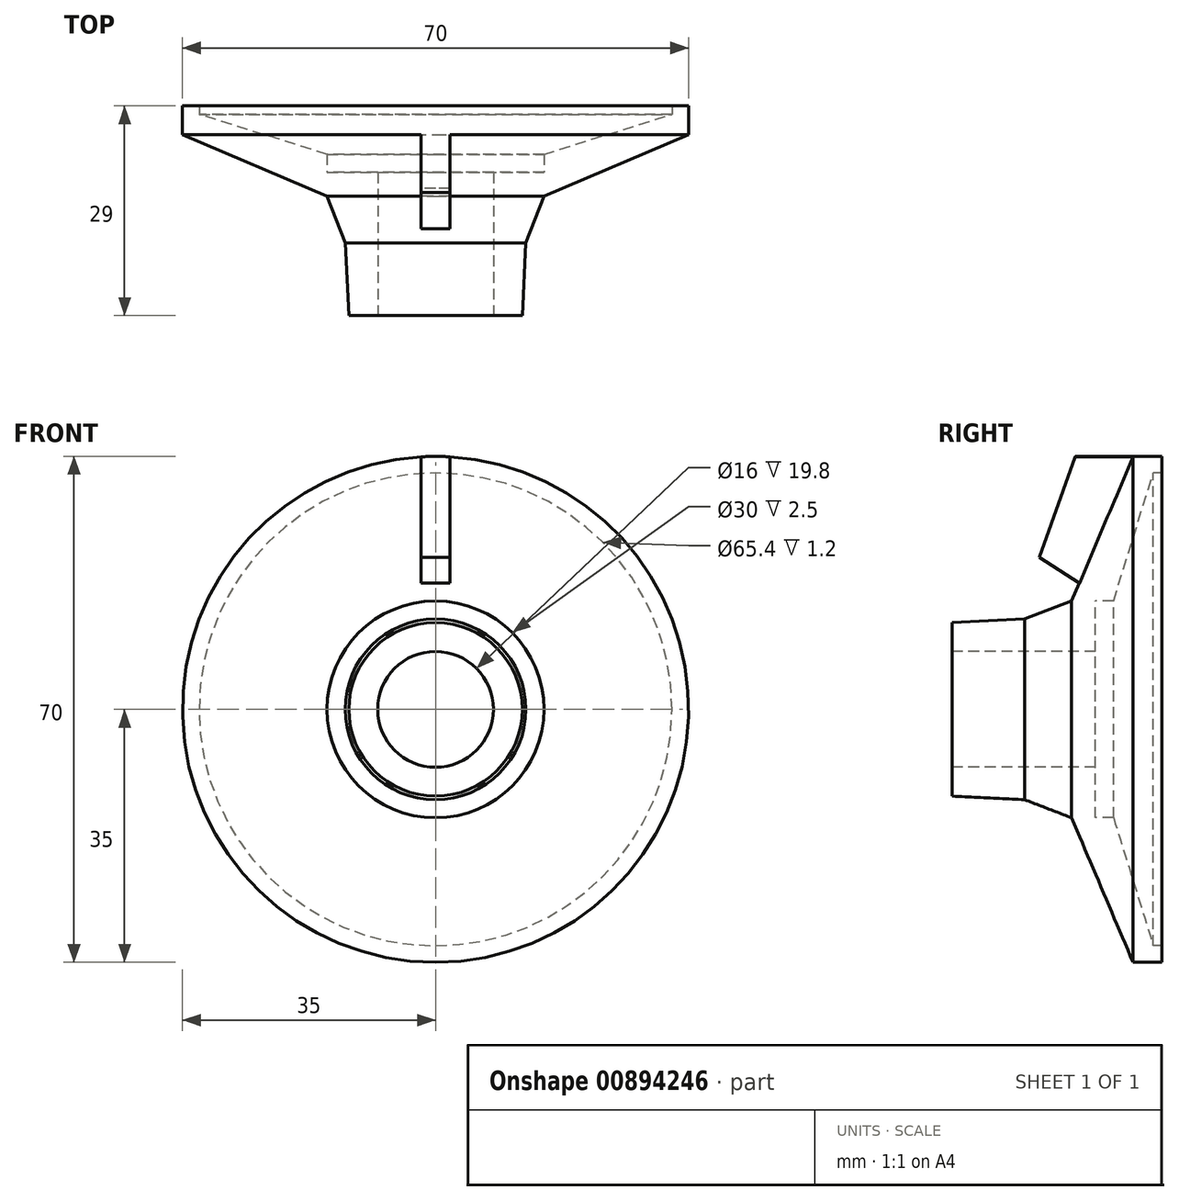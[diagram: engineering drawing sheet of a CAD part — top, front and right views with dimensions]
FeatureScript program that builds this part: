
annotation { "Feature Type Name" : "Feature", "Feature Type Description" : "" }
export const myFeature = defineFeature(function(context is Context, id is Id, definition is map)
    precondition{}
    {
        {
            var Q0;
            Q0=qCreatedBy(makeId("Right.planeOp"),FACE);
            var sketch = newSketch(context, id + "F0", { "sketchPlane" : qUnion([Q0])});
            skLineSegment(sketch, "E0", {"start": v(0, 0) * mm, "end": v(0, 8) * mm, "construction": true});
            skLineSegment(sketch, "E1", {"start": v(0, 8) * mm, "end": v(0, 12) * mm});
            skLineSegment(sketch, "E2", {"start": v(0, 0) * mm, "end": v(29, 0) * mm});
            skLineSegment(sketch, "E3", {"start": v(0, 8) * mm, "end": v(19.8, 8) * mm});
            skLineSegment(sketch, "E4", {"start": v(0, 12) * mm, "end": v(10, 12.5) * mm});
            skLineSegment(sketch, "E5", {"start": v(10, 12.5) * mm, "end": v(16.5, 15) * mm});
            skLineSegment(sketch, "E6", {"start": v(16.5, 15) * mm, "end": v(25, 35) * mm});
            skLineSegment(sketch, "E7", {"start": v(25, 35) * mm, "end": v(29, 35) * mm});
            skLineSegment(sketch, "E8", {"start": v(29, 35) * mm, "end": v(29, 32.7) * mm});
            skLineSegment(sketch, "E9", {"start": v(29, 32.7) * mm, "end": v(27.8, 32.7) * mm});
            skLineSegment(sketch, "E10", {"start": v(27.8, 32.7) * mm, "end": v(22.3, 15) * mm});
            skLineSegment(sketch, "E11", {"start": v(22.3, 15) * mm, "end": v(19.8, 15) * mm});
            skLineSegment(sketch, "E12", {"start": v(19.8, 15) * mm, "end": v(19.8, 8) * mm});
            skSolve(sketch);
        }
        {
            var Q0;
            Q0=makeQuery(id+"F0.imprint","IMPRINT",FACE,{"disambiguationData":[TD([[makeQuery(id+"F0.imprint","IMPRINT",EDGE,{"derivedFrom":sQuery(id+"F0.wireOp",EDGE,"E1")}),-1.0]])]});
            var Q1;
            Q1=sQuery(id+"F0.wireOp",EDGE,"E2");
            revolve(context, id + "F1", {"surfaceOperationType" : NewSurfaceOperationType.NEW, "entities" : qUnion([Q0]), "axis" : qUnion([Q1]), "revolveType" : RevolveType.FULL});
        }
        {
            var Q0;
            Q0=qCreatedBy(makeId("Right.planeOp"),FACE);
            var sketch = newSketch(context, id + "F2", { "sketchPlane" : qUnion([Q0])});
            skLineSegment(sketch, "E13", {"start": v(25, 35) * mm, "end": v(17, 35) * mm});
            skLineSegment(sketch, "E14", {"start": v(17, 35) * mm, "end": v(12, 21) * mm});
            skLineSegment(sketch, "E15", {"start": v(12, 21) * mm, "end": v(17.56, 17.5) * mm});
            skLineSegment(sketch, "E16", {"start": v(17.56, 17.5) * mm, "end": v(25, 35) * mm, "construction": true});
            skLineSegment(sketch, "E17", {"start": v(0, 0) * mm, "end": v(25, 0) * mm, "construction": true});
            skLineSegment(sketch, "E18", {"start": v(25, 0) * mm, "end": v(25, 35) * mm, "construction": true});
            skLineSegment(sketch, "E19", {"start": v(17.56, 17.5) * mm, "end": v(19.56, 17.5) * mm});
            skLineSegment(sketch, "E20", {"start": v(25, 35) * mm, "end": v(27, 35) * mm});
            skLineSegment(sketch, "E21", {"start": v(27, 35) * mm, "end": v(19.56, 17.5) * mm});
            skSolve(sketch);
        }
        {
            var Q0;
            Q0=makeQuery(id+"F2.imprint","IMPRINT",FACE,{"disambiguationData":[TD([[makeQuery(id+"F2.imprint","IMPRINT",EDGE,{"derivedFrom":sQuery(id+"F2.wireOp",EDGE,"E13")}),1.0]])]});
            extrude(context, id + "F3", {"entities" : qUnion([Q0]), "operationType" : NewBodyOperationType.ADD, "depth" : 4 * mm, "offsetDistance" : 25 * mm, "symmetric" : true});
        }
        {
            var Q0;
            Q0=qCreatedBy(makeId("Right.planeOp"),FACE);
            var sketch = newSketch(context, id + "F4", { "sketchPlane" : qUnion([Q0])});
            skLineSegment(sketch, "E22", {"start": v(0, 0) * mm, "end": v(29, 0) * mm});
            skLineSegment(sketch, "E23", {"start": v(29, 0) * mm, "end": v(29, 35) * mm, "construction": true});
            skLineSegment(sketch, "E24", {"start": v(29, 35) * mm, "end": v(16, 35) * mm});
            skLineSegment(sketch, "E25", {"start": v(16, 35) * mm, "end": v(16, 37) * mm});
            skLineSegment(sketch, "E26", {"start": v(16, 37) * mm, "end": v(29, 37) * mm});
            skLineSegment(sketch, "E27", {"start": v(29, 37) * mm, "end": v(29, 35) * mm});
            skSolve(sketch);
        }
        {
            var Q0;
            Q0=makeQuery(id+"F4.imprint","IMPRINT",FACE,{"disambiguationData":[TD([[makeQuery(id+"F4.imprint","IMPRINT",EDGE,{"derivedFrom":sQuery(id+"F4.wireOp",EDGE,"E24")}),-1.0]])]});
            var Q1;
            Q1=sQuery(id+"F4.wireOp",EDGE,"E22");
            revolve(context, id + "F5", {"operationType" : NewBodyOperationType.REMOVE, "surfaceOperationType" : NewSurfaceOperationType.NEW, "entities" : qUnion([Q0]), "axis" : qUnion([Q1]), "revolveType" : RevolveType.FULL, "oppositeDirection" : true});
        }
    });
